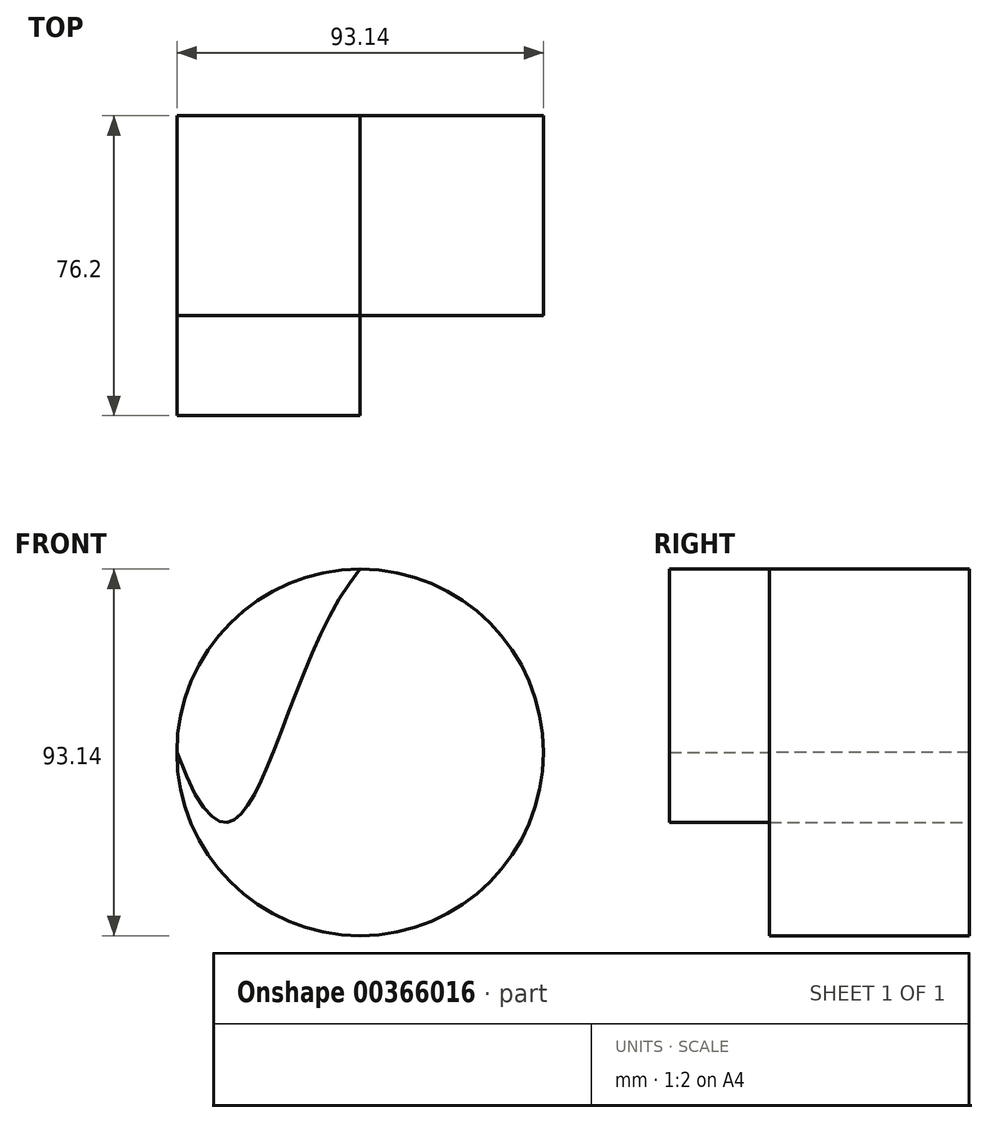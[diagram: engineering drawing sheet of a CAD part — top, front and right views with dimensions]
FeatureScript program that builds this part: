
annotation { "Feature Type Name" : "Feature", "Feature Type Description" : "" }
export const myFeature = defineFeature(function(context is Context, id is Id, definition is map)
    precondition{}
    {
        {
            var Q0;
            Q0=qCreatedBy(makeId("Front.planeOp"),FACE);
            var sketch = newSketch(context, id + "F0", { "sketchPlane" : qUnion([Q0])});
            skCircle(sketch, "E0", {"center": v(0, 0) * mm, "radius": 46.57 * mm});
            skLineSegment(sketch, "E1.bottom", {"start": v(91.96, -19.68) * mm, "end": v(144.31, -19.68) * mm});
            skLineSegment(sketch, "E1.top", {"start": v(91.96, -50.22) * mm, "end": v(144.31, -50.22) * mm});
            skLineSegment(sketch, "E1.left", {"start": v(91.96, -19.68) * mm, "end": v(91.96, -50.22) * mm});
            skLineSegment(sketch, "E1.right", {"start": v(144.31, -19.68) * mm, "end": v(144.31, -50.22) * mm});
            skFitSpline(sketch, "E2", {"points": [v(91.96, -19.68) * mm, v(0, 46.57) * mm, v(-46.57, 0) * mm], "startDerivative": vector(-37.26, 280.35) * mm, "endDerivative": vector(-132.1, 352.94) * mm});
            skArc(sketch, "E3", {"start": v(-46.57, 0) * mm, "mid": v(5.07, -73.72) * mm, "end": v(91.96, -50.22) * mm});
            skSolve(sketch);
        }
        {
            var Q0;
            {var subQ0=sQuery(id+"F0.wireOp",EDGE,"E2");var subQ1=sQuery(id+"F0.wireOp",EDGE,"E0");var subQ3=makeQuery(id+"F0.imprint","INTERSECT",VERTEX,{"derivedFrom":[subQ1,subQ0]});Q0=makeQuery(id+"F0.imprint","IMPRINT",FACE,{"disambiguationData":[TD([[makeQuery(id+"F0.imprint","IMPRINT",EDGE,{"disambiguationData":[TD([[subQ3,-1.0]])],"derivedFrom":subQ1}),1.0]])]});}
            extrude(context, id + "F1", {"entities" : qUnion([Q0]), "depth" : 25.4 * mm});
        }
        {
            var Q0;
            {var subQ0=sQuery(id+"F0.wireOp",EDGE,"E2");var subQ1=sQuery(id+"F0.wireOp",EDGE,"E0");var subQ3=makeQuery(id+"F0.imprint","INTERSECT",VERTEX,{"derivedFrom":[subQ1,subQ0]});Q0=makeQuery(id+"F0.imprint","IMPRINT",FACE,{"disambiguationData":[TD([[makeQuery(id+"F0.imprint","IMPRINT",EDGE,{"disambiguationData":[TD([[subQ3,1.0]])],"derivedFrom":subQ1}),1.0]])]});}
            extrude(context, id + "F2", {"entities" : qUnion([Q0]), "operationType" : NewBodyOperationType.ADD, "oppositeDirection" : true, "depth" : 50.8 * mm});
        }
    });
